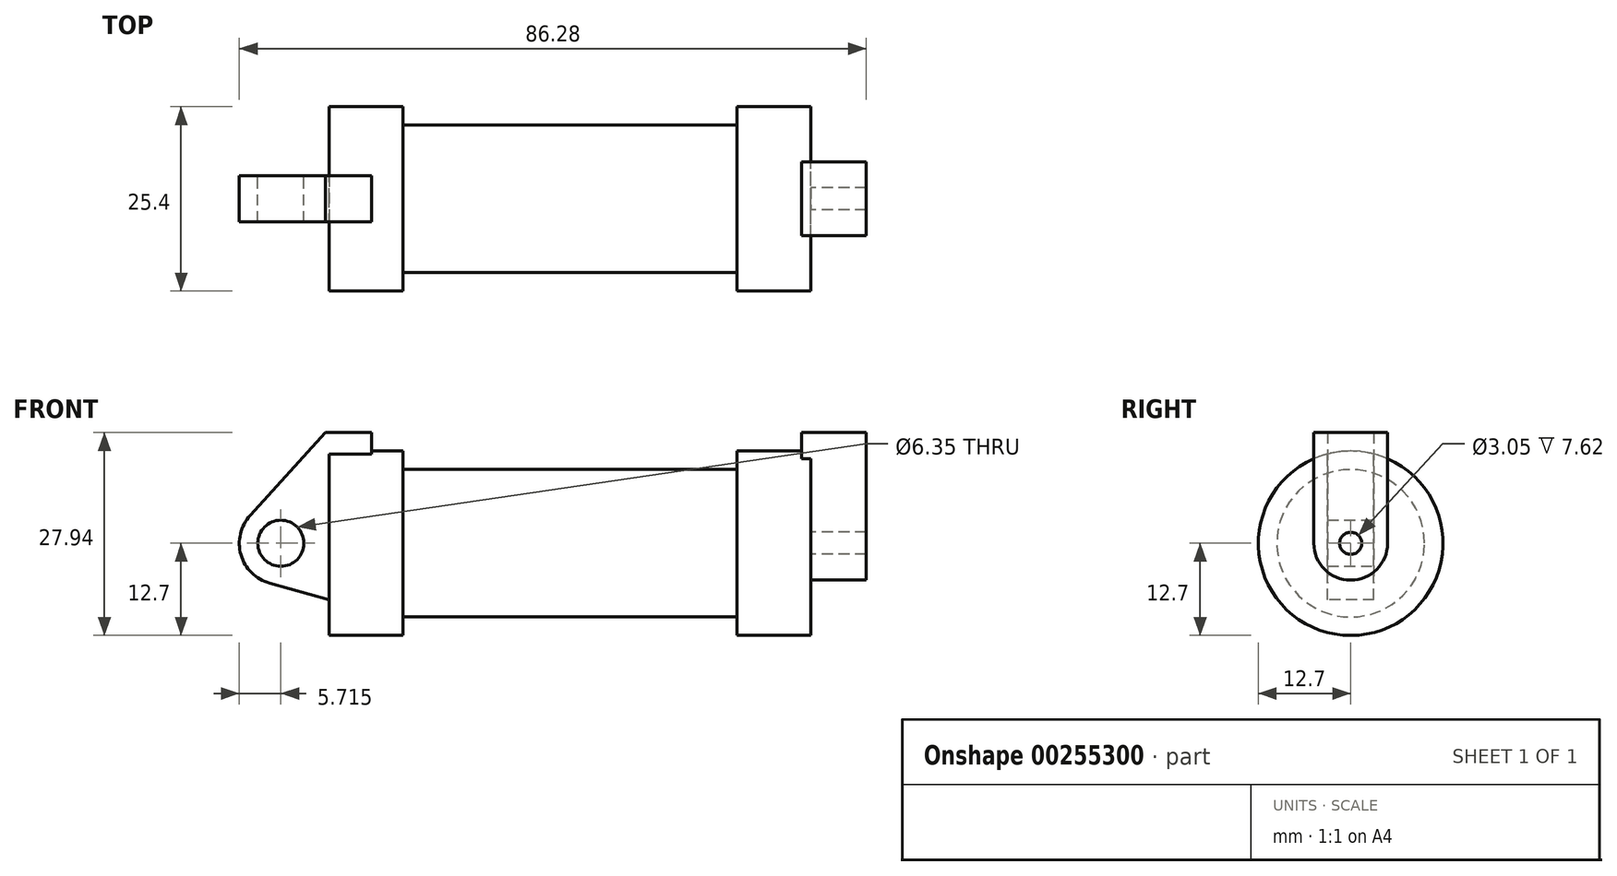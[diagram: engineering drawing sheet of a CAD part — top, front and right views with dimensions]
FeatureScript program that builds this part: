
annotation { "Feature Type Name" : "Feature", "Feature Type Description" : "" }
export const myFeature = defineFeature(function(context is Context, id is Id, definition is map)
    precondition{}
    {
        {
            var Q0;
            Q0=qCreatedBy(makeId("Front.planeOp"),FACE);
            var sketch = newSketch(context, id + "F0", { "sketchPlane" : qUnion([Q0])});
            skLineSegment(sketch, "E0", {"start": v(0, 0) * mm, "end": v(0, 12.7) * mm});
            skLineSegment(sketch, "E1", {"start": v(0, 12.7) * mm, "end": v(10.16, 12.7) * mm});
            skLineSegment(sketch, "E2", {"start": v(10.16, 12.7) * mm, "end": v(10.16, 10.16) * mm});
            skLineSegment(sketch, "E3", {"start": v(10.16, 10.16) * mm, "end": v(56.13, 10.16) * mm});
            skLineSegment(sketch, "E4", {"start": v(56.13, 10.16) * mm, "end": v(56.13, 12.7) * mm});
            skLineSegment(sketch, "E5", {"start": v(56.13, 12.7) * mm, "end": v(66.3, 12.7) * mm});
            skLineSegment(sketch, "E6", {"start": v(66.3, 12.7) * mm, "end": v(66.3, 0) * mm});
            skLineSegment(sketch, "E7", {"start": v(66.3, 0) * mm, "end": v(0, 0) * mm});
            skLineSegment(sketch, "E8", {"start": v(5.84, 15.24) * mm, "end": v(-0.5, 15.24) * mm});
            skLineSegment(sketch, "E9", {"start": v(-0.5, 15.24) * mm, "end": v(-10.88, 3.85) * mm});
            skLineSegment(sketch, "E10", {"start": v(0, 0) * mm, "end": v(-6.65, 0) * mm});
            skCircle(sketch, "E11", {"center": v(-6.65, 0) * mm, "radius": 5.72 * mm});
            skCircle(sketch, "E12", {"center": v(-6.65, 0) * mm, "radius": 3.18 * mm});
            skLineSegment(sketch, "E13", {"start": v(5.84, 15.24) * mm, "end": v(5.84, -9.4) * mm});
            skLineSegment(sketch, "E14", {"start": v(5.84, -9.4) * mm, "end": v(-8.18, -5.5) * mm});
            skSolve(sketch);
        }
        {
            var Q0;
            {var subQ3=sQuery(id+"F0.wireOp",EDGE,"E0");Q0=makeQuery(id+"F0.imprint","IMPRINT",FACE,{"disambiguationData":[TD([[makeQuery(id+"F0.imprint","IMPRINT",EDGE,{"derivedFrom":subQ3}),1.0]])]});}
            var Q1;
            {var subQ0=sQuery(id+"F0.wireOp",EDGE,"E14");Q1=makeQuery(id+"F0.imprint","IMPRINT",FACE,{"disambiguationData":[TD([[makeQuery(id+"F0.imprint","IMPRINT",EDGE,{"derivedFrom":subQ0}),-1.0]])]});}
            var Q2;
            {var subQ4=sQuery(id+"F0.wireOp",EDGE,"E12");Q2=makeQuery(id+"F0.imprint","IMPRINT",FACE,{"disambiguationData":[TD([[makeQuery(id+"F0.imprint","IMPRINT",EDGE,{"derivedFrom":subQ4}),-1.0]])]});}
            var Q3;
            {var subQ0=sQuery(id+"F0.wireOp",EDGE,"E0");Q3=makeQuery(id+"F0.imprint","IMPRINT",FACE,{"disambiguationData":[TD([[makeQuery(id+"F0.imprint","IMPRINT",EDGE,{"derivedFrom":subQ0}),-1.0]])]});}
            extrude(context, id + "F1", {"entities" : qUnion([Q0, Q1, Q2, Q3]), "endBound" : BoundingType.SYMMETRIC, "depth" : 6.35 * mm});
        }
        {
            var Q0;
            {var subQ0=sQuery(id+"F0.wireOp",EDGE,"E0");Q0=makeQuery(id+"F0.imprint","IMPRINT",FACE,{"disambiguationData":[TD([[makeQuery(id+"F0.imprint","IMPRINT",EDGE,{"derivedFrom":subQ0}),-1.0]])]});}
            var Q1;
            {var subQ0=sQuery(id+"F0.wireOp",EDGE,"E2");Q1=makeQuery(id+"F0.imprint","IMPRINT",FACE,{"disambiguationData":[TD([[makeQuery(id+"F0.imprint","IMPRINT",EDGE,{"derivedFrom":subQ0}),-1.0]])]});}
            var Q2;
            Q2=sQuery(id+"F0.wireOp",EDGE,"E7");
            revolve(context, id + "F2", {"operationType" : NewBodyOperationType.ADD, "entities" : qUnion([Q0, Q1]), "axis" : qUnion([Q2]), "revolveType" : RevolveType.FULL});
        }
        {
            var Q0;
            Q0=makeQuery(id+"F2.opRevolve","SWEPT_FACE",FACE,{"disambiguationData":[OSD([sQuery(id+"F0.wireOp",EDGE,"E6")])]});
            var sketch = newSketch(context, id + "F3", { "sketchPlane" : qUnion([Q0])});
            skCircle(sketch, "E15", {"center": v(0, 0) * mm, "radius": 1.52 * mm});
            skCircle(sketch, "E16", {"center": v(0, 0) * mm, "radius": 5.08 * mm});
            skLineSegment(sketch, "E17", {"start": v(0, 0) * mm, "end": v(-5.08, 0) * mm});
            skLineSegment(sketch, "E18", {"start": v(0, 0) * mm, "end": v(5.08, 0) * mm});
            skLineSegment(sketch, "E19.0", {"start": v(-3.18, 15.24) * mm, "end": v(3.17, 15.24) * mm});
            skLineSegment(sketch, "E20", {"start": v(-5.08, 0) * mm, "end": v(-5.08, 15.24) * mm});
            skPoint(sketch, "E20.endSnap0", {"position": v(0, 15.24) * mm});
            skLineSegment(sketch, "E21", {"start": v(5.08, 0) * mm, "end": v(5.08, 15.24) * mm});
            skLineSegment(sketch, "E22", {"start": v(5.08, 15.24) * mm, "end": v(-5.08, 15.24) * mm});
            skSolve(sketch);
        }
        {
            var Q0;
            {var subQ0=sQuery(id+"F3.wireOp",EDGE,"E22");var subQ1=sQuery(id+"F3.wireOp",EDGE,"E20");var subQ2=makeQuery(id+"F3.imprint","INTERSECT",VERTEX,{"derivedFrom":[subQ1,subQ0]});Q0=makeQuery(id+"F3.imprint","IMPRINT",FACE,{"disambiguationData":[TD([[makeQuery(id+"F3.imprint","IMPRINT",EDGE,{"disambiguationData":[TD([[subQ2,1.0]])],"derivedFrom":subQ0}),1.0]])]});}
            var Q1;
            {var subQ0=sQuery(id+"F3.wireOp",EDGE,"E20");var subQ1=sQuery(id+"F3.wireOp",EDGE,"E16");var subQ2=makeQuery(id+"F3.imprint","INTERSECT",VERTEX,{"derivedFrom":[subQ1,sQuery(id+"F3.wireOp",EDGE,"E17"),subQ0]});Q1=makeQuery(id+"F3.imprint","IMPRINT",FACE,{"disambiguationData":[TD([[makeQuery(id+"F3.imprint","IMPRINT",EDGE,{"disambiguationData":[TD([[subQ2,1.0]])],"derivedFrom":subQ1}),-1.0]])]});}
            var Q2;
            {var subQ0=sQuery(id+"F3.wireOp",EDGE,"E17");var subQ1=sQuery(id+"F3.wireOp",EDGE,"E15");var subQ2=makeQuery(id+"F3.imprint","INTERSECT",VERTEX,{"derivedFrom":[subQ1,subQ0]});Q2=makeQuery(id+"F3.imprint","IMPRINT",FACE,{"disambiguationData":[TD([[makeQuery(id+"F3.imprint","IMPRINT",EDGE,{"disambiguationData":[TD([[subQ2,1.0]])],"derivedFrom":subQ1}),-1.0]])]});}
            var Q3;
            {var subQ0=sQuery(id+"F3.wireOp",EDGE,"E17");var subQ1=sQuery(id+"F3.wireOp",EDGE,"E15");var subQ2=makeQuery(id+"F3.imprint","INTERSECT",VERTEX,{"derivedFrom":[subQ1,subQ0]});Q3=makeQuery(id+"F3.imprint","IMPRINT",FACE,{"disambiguationData":[TD([[makeQuery(id+"F3.imprint","IMPRINT",EDGE,{"disambiguationData":[TD([[subQ2,-1.0]])],"derivedFrom":subQ1}),-1.0]])]});}
            extrude(context, id + "F4", {"entities" : qUnion([Q0, Q1, Q2, Q3]), "operationType" : NewBodyOperationType.ADD, "depth" : 7.62 * mm});
        }
        {
            var Q0;
            Q0=makeQuery(id+"F4.opExtrude","CAP_FACE",FACE,{"disambiguationData":[OSD([sQuery(id+"F3.wireOp",EDGE,"E15"),sQuery(id+"F3.wireOp",EDGE,"E16"),sQuery(id+"F3.wireOp",EDGE,"E20"),sQuery(id+"F3.wireOp",EDGE,"E21"),sQuery(id+"F3.wireOp",EDGE,"E22")])],"isStart":true});
            extrude(context, id + "F5", {"entities" : qUnion([Q0]), "operationType" : NewBodyOperationType.ADD, "depth" : 1.27 * mm});
        }
    });
